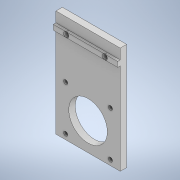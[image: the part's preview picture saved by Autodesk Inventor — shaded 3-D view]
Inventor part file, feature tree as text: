
AUTODESK INVENTOR PART (.ipt)
format: ipt  version: 2021 (Build 250183000, 183)  size: 167,936 bytes
history: native  units: mm
features: extrude x3, sketch x3, projected_geometry x2
ambient origin geometry x8: Origin, YZ Plane, XZ Plane, XY Plane, X Axis, Y Axis, Z Axis, Center Point
bodies: Solid1 (feature_tree)
feature tree (8):
  extrude  "Extrusion1"  Depth=166.0mm
  extrude  "Extrusion2"  Depth=43.0mm
  extrude  "Extrusion3"  Depth=8.0mm
  sketch  "Sketch1"  dims[d0=100.0mm d1=166.0mm]
  sketch  "Sketch2"  dims[d2=60.0mm d3=43.0mm]
  projected_geometry  "Projected Loop1"
  sketch  "Sketch3"  dims[d4=8.0mm d5=8.0mm d6=20.0mm d7=20.0mm d8=20.0mm d9=20.0mm d10=6.5mm d11=6.5mm d12=6.5mm d13=6.5mm d14=69.6mm d15=69.6mm d16=69.6mm d17=69.6mm d18=0.0mm d19=0.0mm d20=34.8mm d21=34.8mm d22=69.0mm d23=20.0mm d24=0.0mm d25=4.0mm d26=4.0mm d27=4.0mm d28=0.0mm d29=6.0mm d30=0.0mm]
  projected_geometry  "Projected Loop2"
